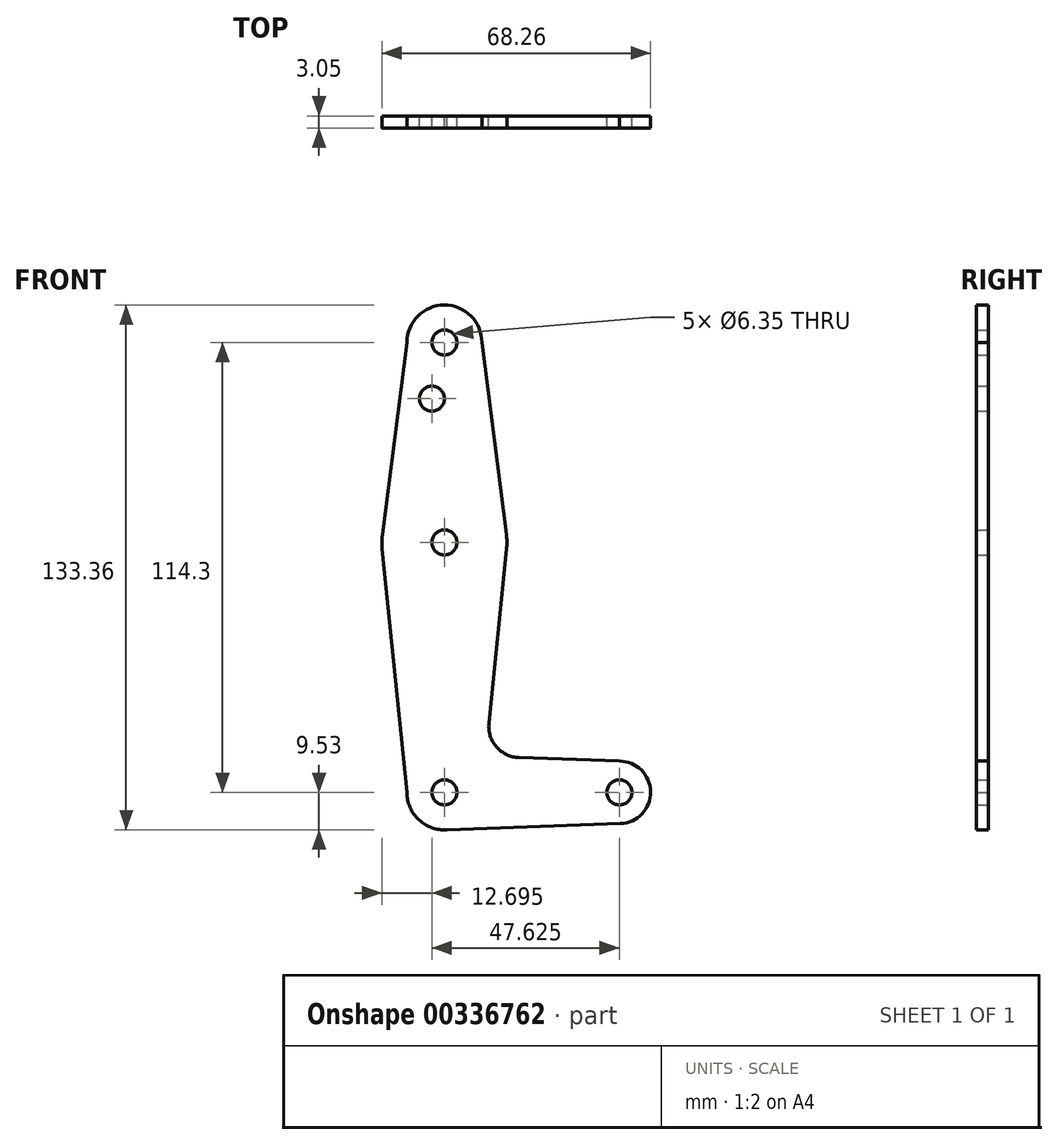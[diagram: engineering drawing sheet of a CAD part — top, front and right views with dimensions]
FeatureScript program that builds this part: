
annotation { "Feature Type Name" : "Feature", "Feature Type Description" : "" }
export const myFeature = defineFeature(function(context is Context, id is Id, definition is map)
    precondition{}
    {
        {
            var Q0;
            Q0=qCreatedBy(makeId("Front.planeOp"),FACE);
            var sketch = newSketch(context, id + "F0", { "sketchPlane" : qUnion([Q0])});
            skLineSegment(sketch, "E0", {"start": v(0, 0) * mm, "end": v(0, 114.3) * mm});
            skLineSegment(sketch, "E1", {"start": v(0, 0) * mm, "end": v(44.45, 0) * mm});
            skCircle(sketch, "E2", {"center": v(0, 114.3) * mm, "radius": 9.53 * mm});
            skCircle(sketch, "E3", {"center": v(0, 63.5) * mm, "radius": 15.88 * mm});
            skCircle(sketch, "E4", {"center": v(0, 0) * mm, "radius": 9.53 * mm});
            skCircle(sketch, "E5", {"center": v(44.45, 0) * mm, "radius": 7.94 * mm});
            skLineSegment(sketch, "E6", {"start": v(-9.52, 114.3) * mm, "end": v(-15.75, 65.5) * mm});
            skLineSegment(sketch, "E7", {"start": v(9.53, 114.3) * mm, "end": v(15.75, 65.5) * mm});
            skLineSegment(sketch, "E8", {"start": v(-9.53, 0) * mm, "end": v(-15.8, 61.9) * mm});
            skLineSegment(sketch, "E9", {"start": v(15.8, 61.9) * mm, "end": v(11.3, 17.6) * mm});
            skLineSegment(sketch, "E10", {"start": v(18.93, 8.85) * mm, "end": v(44.45, 7.94) * mm});
            skLineSegment(sketch, "E11", {"start": v(0, -9.53) * mm, "end": v(44.73, -7.93) * mm});
            skCircle(sketch, "E12", {"center": v(0, 114.3) * mm, "radius": 3.18 * mm});
            skCircle(sketch, "E13", {"center": v(0, 63.5) * mm, "radius": 3.18 * mm});
            skCircle(sketch, "E14", {"center": v(0, 0) * mm, "radius": 3.18 * mm});
            skCircle(sketch, "E15", {"center": v(44.45, 0) * mm, "radius": 3.18 * mm});
            skCircle(sketch, "E16", {"center": v(-3.18, 100.03) * mm, "radius": 3.18 * mm});
            skArc(sketch, "E17.filletArc", {"start": v(11.3, 17.6) * mm, "mid": v(13.22, 11.57) * mm, "end": v(18.93, 8.85) * mm});
            skSolve(sketch);
        }
        {
            var Q0;
            Q0 = qSketchRegion(id + "F0", true);
            var Q1;
            {var subQ0=sQuery(id+"F0.wireOp",EDGE,"E14");var subQ1=sQuery(id+"F0.wireOp",EDGE,"E0");var subQ2=makeQuery(id+"F0.imprint","INTERSECT",VERTEX,{"derivedFrom":[subQ1,subQ0]});Q1=makeQuery(id+"F0.imprint","IMPRINT",FACE,{"disambiguationData":[TD([[makeQuery(id+"F0.imprint","IMPRINT",EDGE,{"disambiguationData":[TD([[subQ2,-1.0]])],"derivedFrom":subQ1}),-1.0]])]});}
            extrude(context, id + "F1", {"entities" : qUnion([Q0, Q1]), "depth" : 3.05 * mm});
        }
    });
